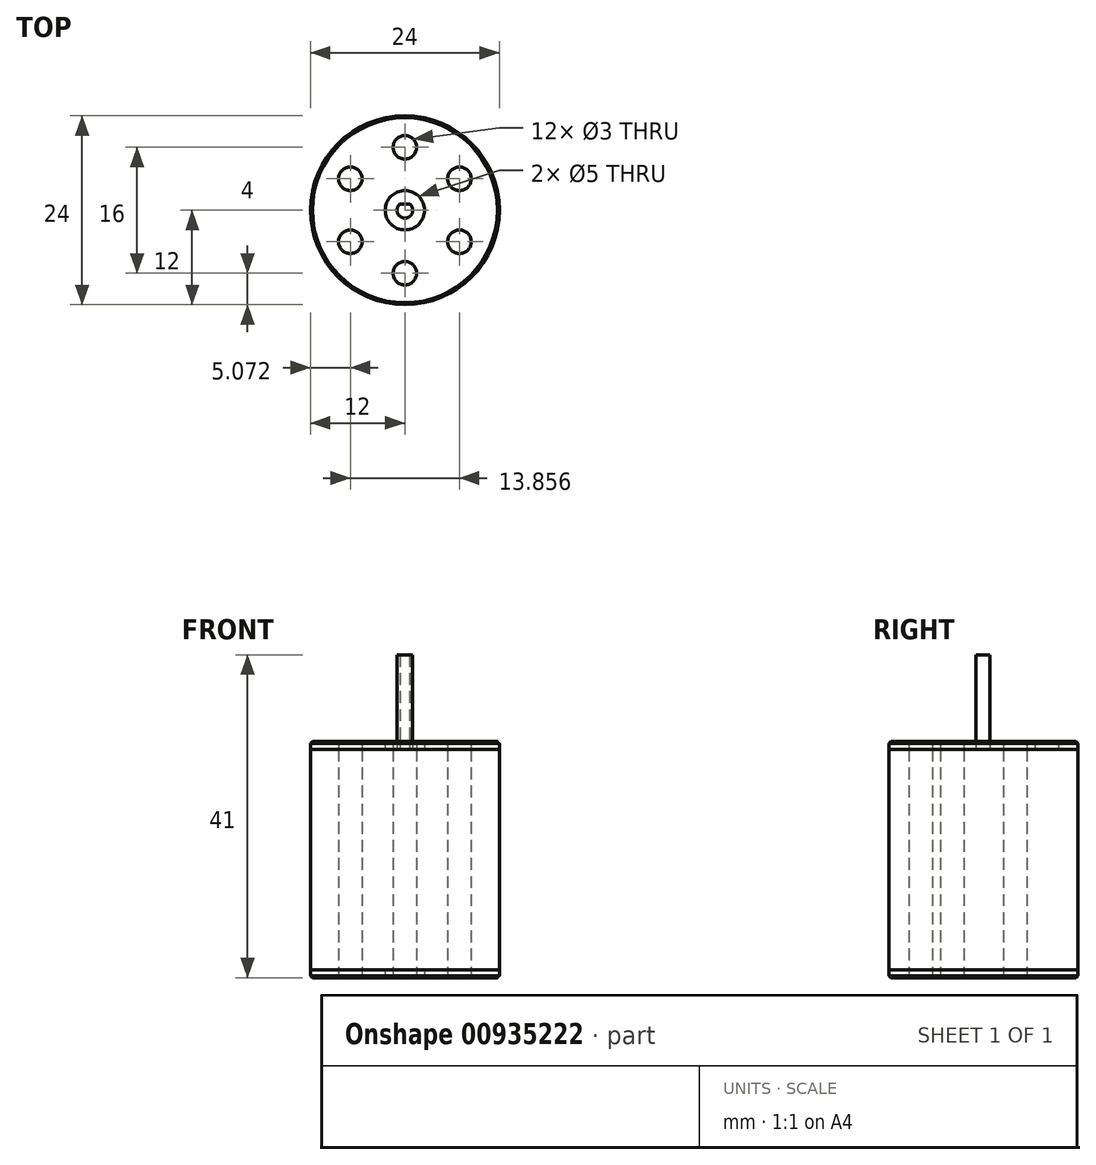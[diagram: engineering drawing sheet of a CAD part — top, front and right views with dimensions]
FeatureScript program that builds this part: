
annotation { "Feature Type Name" : "Feature", "Feature Type Description" : "" }
export const myFeature = defineFeature(function(context is Context, id is Id, definition is map)
    precondition{}
    {
        {
            assignVariable(context, id + "F0", {"name" : "bodyHeight", "anyValue" : 30});
        }
        {
            assignVariable(context, id + "F1", {"name" : "shaftHeight", "anyValue" : 12});
        }
        {
            var Q0;
            Q0=qCreatedBy(makeId("Top.planeOp"),FACE);
            var sketch = newSketch(context, id + "F2", { "sketchPlane" : qUnion([Q0])});
            skCircle(sketch, "E0", {"center": v(0, 0) * mm, "radius": 12 * mm});
            skCircle(sketch, "E1", {"center": v(0, 8) * mm, "radius": 1.5 * mm});
            skCircle(sketch, "E2", {"center": v(0, 0) * mm, "radius": 1 * mm});
            skLineSegment(sketch, "E3", {"start": v(-0.6, 0.8) * mm, "end": v(0.6, 0.8) * mm});
            skCircle(sketch, "E4", {"center": v(0, 0) * mm, "radius": 2.5 * mm});
            skCircle(sketch, "E5.MirrorC", {"center": v(0, -8) * mm, "radius": 1.5 * mm});
            skLineSegment(sketch, "E6", {"start": v(0, 0) * mm, "end": v(10.95, 10.95) * mm, "construction": true});
            skCircle(sketch, "E7", {"center": v(-6.93, 4) * mm, "radius": 1.5 * mm});
            skCircle(sketch, "E8", {"center": v(6.93, -4) * mm, "radius": 1.5 * mm});
            skLineSegment(sketch, "E9", {"start": v(6.93, -4) * mm, "end": v(-6.93, 4) * mm, "construction": true});
            skCircle(sketch, "E10.MirrorC", {"center": v(6.93, 4) * mm, "radius": 1.5 * mm});
            skCircle(sketch, "E11.MirrorC", {"center": v(-6.93, -4) * mm, "radius": 1.5 * mm});
            skSolve(sketch);
        }
        {
            var Q0;
            Q0=makeQuery(id+"F2.imprint","IMPRINT",FACE,{"disambiguationData":[TD([[makeQuery(id+"F2.imprint","IMPRINT",EDGE,{"derivedFrom":sQuery(id+"F2.wireOp",EDGE,"E7")}),1.0]])]});
            var Q1;
            Q1=makeQuery(id+"F2.imprint","IMPRINT",FACE,{"disambiguationData":[TD([[makeQuery(id+"F2.imprint","IMPRINT",EDGE,{"derivedFrom":sQuery(id+"F2.wireOp",EDGE,"E11.MirrorC")}),-1.0]])]});
            var Q2;
            Q2=makeQuery(id+"F2.imprint","IMPRINT",FACE,{"disambiguationData":[TD([[makeQuery(id+"F2.imprint","IMPRINT",EDGE,{"derivedFrom":sQuery(id+"F2.wireOp",EDGE,"E5.MirrorC")}),-1.0]])]});
            var Q3;
            Q3=makeQuery(id+"F2.imprint","IMPRINT",FACE,{"disambiguationData":[TD([[makeQuery(id+"F2.imprint","IMPRINT",EDGE,{"derivedFrom":sQuery(id+"F2.wireOp",EDGE,"E8")}),1.0]])]});
            var Q4;
            Q4=makeQuery(id+"F2.imprint","IMPRINT",FACE,{"disambiguationData":[TD([[makeQuery(id+"F2.imprint","IMPRINT",EDGE,{"derivedFrom":sQuery(id+"F2.wireOp",EDGE,"E10.MirrorC")}),-1.0]])]});
            var Q5;
            Q5=makeQuery(id+"F2.imprint","IMPRINT",FACE,{"disambiguationData":[TD([[makeQuery(id+"F2.imprint","IMPRINT",EDGE,{"derivedFrom":sQuery(id+"F2.wireOp",EDGE,"E1")}),1.0]])]});
            var Q6;
            Q6=makeQuery(id+"F2.imprint","IMPRINT",FACE,{"disambiguationData":[TD([[makeQuery(id+"F2.imprint","IMPRINT",EDGE,{"derivedFrom":sQuery(id+"F2.wireOp",EDGE,"E0")}),1.0]])]});
            extrude(context, id + "F3", {"entities" : qUnion([Q0, Q1, Q2, Q3, Q4, Q5, Q6]), "depth" : 1 * mm, "offsetDistance" : 25 * mm});
        }
        {
            var Q0;
            Q0=makeQuery(id+"F2.imprint","IMPRINT",FACE,{"disambiguationData":[TD([[makeQuery(id+"F2.imprint","IMPRINT",EDGE,{"derivedFrom":sQuery(id+"F2.wireOp",EDGE,"E11.MirrorC")}),-1.0]])]});
            var Q1;
            Q1=makeQuery(id+"F2.imprint","IMPRINT",FACE,{"disambiguationData":[TD([[makeQuery(id+"F2.imprint","IMPRINT",EDGE,{"derivedFrom":sQuery(id+"F2.wireOp",EDGE,"E5.MirrorC")}),-1.0]])]});
            var Q2;
            Q2=makeQuery(id+"F2.imprint","IMPRINT",FACE,{"disambiguationData":[TD([[makeQuery(id+"F2.imprint","IMPRINT",EDGE,{"derivedFrom":sQuery(id+"F2.wireOp",EDGE,"E10.MirrorC")}),-1.0]])]});
            var Q3;
            Q3=makeQuery(id+"F2.imprint","IMPRINT",FACE,{"disambiguationData":[TD([[makeQuery(id+"F2.imprint","IMPRINT",EDGE,{"derivedFrom":sQuery(id+"F2.wireOp",EDGE,"E8")}),1.0]])]});
            var Q4;
            Q4=makeQuery(id+"F2.imprint","IMPRINT",FACE,{"disambiguationData":[TD([[makeQuery(id+"F2.imprint","IMPRINT",EDGE,{"derivedFrom":sQuery(id+"F2.wireOp",EDGE,"E0")}),1.0]])]});
            var Q5;
            Q5=makeQuery(id+"F2.imprint","IMPRINT",FACE,{"disambiguationData":[TD([[makeQuery(id+"F2.imprint","IMPRINT",EDGE,{"derivedFrom":sQuery(id+"F2.wireOp",EDGE,"E1")}),1.0]])]});
            var Q6;
            Q6=makeQuery(id+"F2.imprint","IMPRINT",FACE,{"disambiguationData":[TD([[makeQuery(id+"F2.imprint","IMPRINT",EDGE,{"derivedFrom":sQuery(id+"F2.wireOp",EDGE,"E7")}),1.0]])]});
            var Q7;
            Q7=makeQuery(id+"F2.imprint","IMPRINT",FACE,{"disambiguationData":[TD([[makeQuery(id+"F2.imprint","IMPRINT",EDGE,{"derivedFrom":sQuery(id+"F2.wireOp",EDGE,"E4")}),1.0]])]});
            var Q8;
            {var subQ0=sQuery(id+"F2.wireOp",EDGE,"E3");Q8=makeQuery(id+"F2.imprint","IMPRINT",FACE,{"disambiguationData":[TD([[makeQuery(id+"F2.imprint","IMPRINT",EDGE,{"derivedFrom":subQ0}),-1.0]])]});}
            var Q9;
            {var subQ0=sQuery(id+"F2.wireOp",EDGE,"E3");Q9=makeQuery(id+"F2.imprint","IMPRINT",FACE,{"disambiguationData":[TD([[makeQuery(id+"F2.imprint","IMPRINT",EDGE,{"derivedFrom":subQ0}),1.0]])]});}
            var Q10;
            Q10=makeQuery(id+"F3.opExtrude","CAP_FACE",FACE,{"disambiguationData":[OSD([sQuery(id+"F2.wireOp",EDGE,"E0"),sQuery(id+"F2.wireOp",EDGE,"E4")])],"isStart":false});
            extrude(context, id + "F4", {"entities" : qUnion([Q0, Q1, Q2, Q3, Q4, Q5, Q6, Q7, Q8, Q9]), "depth" : (getVariable(context, 'bodyHeight') - 1) * mm, "offsetDistance" : 25 * mm, "hasSecondDirection" : true, "secondDirectionBound" : SecondDirectionBoundingType.UP_TO_SURFACE, "secondDirectionOppositeDirection" : false, "secondDirectionDepth" : 1 * mm, "secondDirectionBoundEntityFace" : qUnion([Q10])});
        }
        {
            var Q0;
            Q0=makeQuery(id+"F2.imprint","IMPRINT",FACE,{"disambiguationData":[TD([[makeQuery(id+"F2.imprint","IMPRINT",EDGE,{"derivedFrom":sQuery(id+"F2.wireOp",EDGE,"E0")}),1.0]])]});
            var Q1;
            Q1=makeQuery(id+"F4.opExtrude","CAP_FACE",FACE,{"disambiguationData":[OSD([sQuery(id+"F2.wireOp",EDGE,"E0")])],"isStart":false});
            var Q2;
            Q2=makeQuery(id+"F4.opExtrude","CAP_FACE",FACE,{"disambiguationData":[OSD([sQuery(id+"F2.wireOp",EDGE,"E0")])],"isStart":false});
            extrude(context, id + "F5", {"entities" : qUnion([Q0]), "endBound" : BoundingType.UP_TO_SURFACE, "depth" : 35 * mm, "endBoundEntityFace" : qUnion([Q1]), "hasOffset" : true, "offsetDistance" : 1 * mm, "offsetOppositeDirection" : true, "hasSecondDirection" : true, "secondDirectionBound" : SecondDirectionBoundingType.UP_TO_SURFACE, "secondDirectionOppositeDirection" : false, "secondDirectionDepth" : 34 * mm, "secondDirectionBoundEntityFace" : qUnion([Q2])});
        }
        {
            var Q0;
            {var subQ0=sQuery(id+"F2.wireOp",EDGE,"E3");Q0=makeQuery(id+"F2.imprint","IMPRINT",FACE,{"disambiguationData":[TD([[makeQuery(id+"F2.imprint","IMPRINT",EDGE,{"derivedFrom":subQ0}),-1.0]])]});}
            var Q1;
            Q1=makeQuery(id+"F4.opExtrude","CAP_FACE",FACE,{"disambiguationData":[OSD([sQuery(id+"F2.wireOp",EDGE,"E0")])],"isStart":false});
            var Q2;
            Q2=makeQuery(id+"F4.opExtrude","CAP_FACE",FACE,{"disambiguationData":[OSD([sQuery(id+"F2.wireOp",EDGE,"E0")])],"isStart":false});
            extrude(context, id + "F6", {"entities" : qUnion([Q0]), "endBound" : BoundingType.UP_TO_SURFACE, "depth" : 47 * mm, "endBoundEntityFace" : qUnion([Q1]), "hasOffset" : true, "offsetDistance" : (getVariable(context, 'shaftHeight')) * mm, "offsetOppositeDirection" : true, "hasSecondDirection" : true, "secondDirectionBound" : SecondDirectionBoundingType.UP_TO_SURFACE, "secondDirectionOppositeDirection" : false, "secondDirectionDepth" : 33 * mm, "secondDirectionBoundEntityFace" : qUnion([Q2])});
        }
        {
            var Q0;
            Q0=makeQuery(id+"F5.opExtrude","CAP_EDGE",EDGE,{"disambiguationData":[OSD([sQuery(id+"F2.wireOp",EDGE,"E0")])],"isStart":false});
            var Q1;
            Q1=makeQuery(id+"F3.opExtrude","CAP_EDGE",EDGE,{"disambiguationData":[OSD([sQuery(id+"F2.wireOp",EDGE,"E0")])],"isStart":true});
            chamfer(context, id + "F7", {"entities" : qUnion([Q0, Q1]), "width" : .25 * mm, "tangentPropagation" : true});
        }
    });
